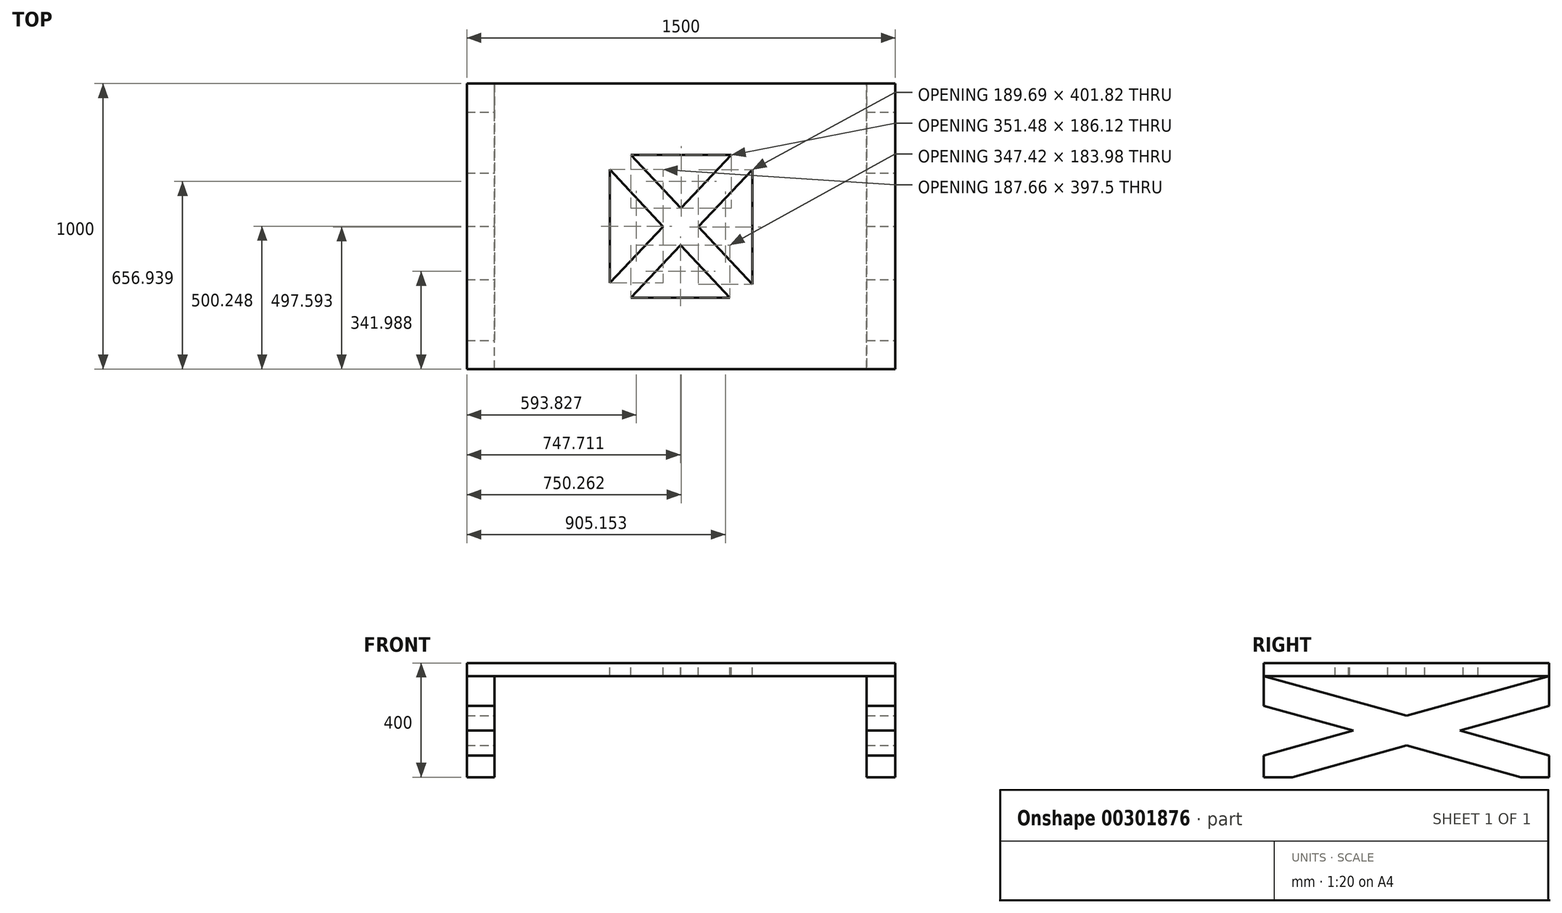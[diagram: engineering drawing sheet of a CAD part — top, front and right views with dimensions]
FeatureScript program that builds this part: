
annotation { "Feature Type Name" : "Feature", "Feature Type Description" : "" }
export const myFeature = defineFeature(function(context is Context, id is Id, definition is map)
    precondition{}
    {
        {
            var Q0;
            Q0=qCreatedBy(makeId("Front.planeOp"),FACE);
            var sketch = newSketch(context, id + "F0", { "sketchPlane" : qUnion([Q0])});
            skLineSegment(sketch, "E0.bottom", {"start": v(-768.36, 54.12) * mm, "end": v(731.64, 54.12) * mm});
            skLineSegment(sketch, "E0.top", {"start": v(-768.36, -345.88) * mm, "end": v(731.64, -345.88) * mm});
            skLineSegment(sketch, "E0.left", {"start": v(-768.36, 54.12) * mm, "end": v(-768.36, -345.88) * mm});
            skLineSegment(sketch, "E0.right", {"start": v(731.64, 54.12) * mm, "end": v(731.64, -345.88) * mm});
            skSolve(sketch);
        }
        {
            var Q0;
            Q0 = qSketchRegion(id + "F0", true);
            extrude(context, id + "F1", {"entities" : qUnion([Q0]), "depth" : 1000 * mm});
        }
        {
            var Q0;
            Q0=makeQuery(id+"F1.opExtrude","SWEPT_FACE",FACE,{"disambiguationData":[OSD([sQuery(id+"F0.wireOp",EDGE,"E0.right")])]});
            var sketch = newSketch(context, id + "F2", { "sketchPlane" : qUnion([Q0])});
            skLineSegment(sketch, "E1", {"start": v(-900, -345.88) * mm, "end": v(0, -95.88) * mm});
            skLineSegment(sketch, "E2", {"start": v(-1000, -269.87) * mm, "end": v(0, 7.9) * mm});
            skLineSegment(sketch, "E3", {"start": v(-100, -345.88) * mm, "end": v(-1000, -95.88) * mm});
            skLineSegment(sketch, "E4", {"start": v(0, -269.87) * mm, "end": v(-1000, 7.9) * mm});
            skLineSegment(sketch, "E5", {"start": v(-1000, 7.9) * mm, "end": v(0, 7.9) * mm});
            skSolve(sketch);
        }
        {
            var Q0;
            {var subQ0=sQuery(id+"F2.wireOp",EDGE,"E5");Q0=makeQuery(id+"F2.imprint","IMPRINT",FACE,{"disambiguationData":[TD([[makeQuery(id+"F2.imprint","IMPRINT",EDGE,{"derivedFrom":subQ0}),-1.0]])]});}
            var Q1;
            {var subQ0=sQuery(id+"F2.wireOp",EDGE,"E1");var subQ3=sQuery(id+"F2.wireOp",EDGE,"E3");var subQ4=makeQuery(id+"F2.imprint","INTERSECT",VERTEX,{"derivedFrom":[subQ0,subQ3]});Q1=makeQuery(id+"F2.imprint","IMPRINT",FACE,{"disambiguationData":[TD([[makeQuery(id+"F2.imprint","IMPRINT",EDGE,{"disambiguationData":[TD([[subQ4,1.0]])],"derivedFrom":subQ0}),-1.0]])]});}
            var Q2;
            {var subQ0=sQuery(id+"F2.wireOp",EDGE,"E1");var subQ1=makeQuery(id+"F1.opExtrude","CAP_EDGE",EDGE,{"disambiguationData":[OSD([sQuery(id+"F0.wireOp",EDGE,"E0.right")])],"isStart":true});var subQ2=makeQuery(id+"F2.imprint","INTERSECT",VERTEX,{"derivedFrom":[subQ1,subQ0]});Q2=makeQuery(id+"F2.imprint","IMPRINT",FACE,{"disambiguationData":[TD([[makeQuery(id+"F2.imprint","IMPRINT",EDGE,{"disambiguationData":[TD([[subQ2,1.0]])],"derivedFrom":subQ0}),-1.0]])]});}
            var Q3;
            {var subQ0=sQuery(id+"F2.wireOp",EDGE,"E2");var subQ1=makeQuery(id+"F1.opExtrude","CAP_EDGE",EDGE,{"disambiguationData":[OSD([sQuery(id+"F0.wireOp",EDGE,"E0.right")])],"isStart":false});var subQ2=makeQuery(id+"F2.imprint","INTERSECT",VERTEX,{"derivedFrom":[subQ1,subQ0]});Q3=makeQuery(id+"F2.imprint","IMPRINT",FACE,{"disambiguationData":[TD([[makeQuery(id+"F2.imprint","IMPRINT",EDGE,{"disambiguationData":[TD([[subQ2,-1.0]])],"derivedFrom":subQ0}),1.0]])]});}
            extrude(context, id + "F3", {"entities" : qUnion([Q0, Q1, Q2, Q3]), "operationType" : NewBodyOperationType.REMOVE, "endBound" : BoundingType.THROUGH_ALL, "oppositeDirection" : true, "depth" : 150 * mm});
        }
        {
            var Q0;
            Q0=makeQuery(id+"F1.opExtrude","CAP_FACE",FACE,{"disambiguationData":[OSD([sQuery(id+"F0.wireOp",EDGE,"E0.bottom"),sQuery(id+"F0.wireOp",EDGE,"E0.top"),sQuery(id+"F0.wireOp",EDGE,"E0.left"),sQuery(id+"F0.wireOp",EDGE,"E0.right")])],"isStart":false});
            var sketch = newSketch(context, id + "F4", { "sketchPlane" : qUnion([Q0])});
            skLineSegment(sketch, "E6", {"start": v(631.64, -345.88) * mm, "end": v(631.64, 8.12) * mm});
            skLineSegment(sketch, "E7", {"start": v(631.64, 8.12) * mm, "end": v(-668.36, 8.12) * mm});
            skLineSegment(sketch, "E8", {"start": v(-668.36, 8.12) * mm, "end": v(-668.36, -345.88) * mm});
            skSolve(sketch);
        }
        {
            var Q0;
            {var subQ0=sQuery(id+"F0.wireOp",EDGE,"E0.bottom");var subQ1=sQuery(id+"F0.wireOp",EDGE,"E0.right");var subQ2=sQuery(id+"F0.wireOp",EDGE,"E0.left");Q0=makeQuery(id+"F3.boolean.opBoolean","SPLIT",FACE,{"disambiguationData":[TD([makeQuery(id+"F1.opExtrude","SWEPT_FACE",FACE,{"disambiguationData":[OSD([subQ0])]})])],"derivedFrom":makeQuery(id+"F1.opExtrude","CAP_FACE",FACE,{"disambiguationData":[OSD([subQ0,sQuery(id+"F0.wireOp",EDGE,"E0.top"),subQ2,subQ1])],"isStart":true})});}
            var sketch = newSketch(context, id + "F5", { "sketchPlane" : qUnion([Q0])});
            skLineSegment(sketch, "E9.bottom", {"start": v(-631.78, 7.9) * mm, "end": v(672.17, 7.9) * mm});
            skLineSegment(sketch, "E9.top", {"start": v(-631.78, -349.34) * mm, "end": v(672.17, -349.34) * mm});
            skLineSegment(sketch, "E9.left", {"start": v(-631.78, 7.9) * mm, "end": v(-631.78, -349.34) * mm});
            skLineSegment(sketch, "E9.right", {"start": v(672.17, 7.9) * mm, "end": v(672.17, -349.34) * mm});
            skSolve(sketch);
        }
        {
            var Q0;
            Q0=makeQuery(id+"F5.imprint","IMPRINT",FACE,{"disambiguationData":[TD([[makeQuery(id+"F5.imprint","IMPRINT",EDGE,{"derivedFrom":sQuery(id+"F5.wireOp",EDGE,"E9.bottom")}),1.0]])]});
            extrude(context, id + "F6", {"entities" : qUnion([Q0]), "operationType" : NewBodyOperationType.REMOVE, "endBound" : BoundingType.THROUGH_ALL, "oppositeDirection" : true, "depth" : 25 * mm});
        }
        {
            var Q0;
            Q0=makeQuery(id+"F1.opExtrude","SWEPT_FACE",FACE,{"disambiguationData":[OSD([sQuery(id+"F0.wireOp",EDGE,"E0.bottom")])]});
            var sketch = newSketch(context, id + "F7", { "sketchPlane" : qUnion([Q0])});
            skLineSegment(sketch, "E10.bottom", {"start": v(231.64, -250) * mm, "end": v(-268.36, -250) * mm});
            skLineSegment(sketch, "E10.top", {"start": v(231.64, -750) * mm, "end": v(-268.36, -750) * mm});
            skLineSegment(sketch, "E10.left", {"start": v(231.64, -250) * mm, "end": v(231.64, -750) * mm});
            skLineSegment(sketch, "E10.right", {"start": v(-268.36, -250) * mm, "end": v(-268.36, -750) * mm});
            skLineSegment(sketch, "E11", {"start": v(231.64, -301.5) * mm, "end": v(-194.36, -750) * mm});
            skLineSegment(sketch, "E12", {"start": v(157.64, -250) * mm, "end": v(-268.36, -698.5) * mm});
            skLineSegment(sketch, "E13", {"start": v(-193.84, -250) * mm, "end": v(231.64, -703.32) * mm});
            skLineSegment(sketch, "E14", {"start": v(-268.36, -301) * mm, "end": v(153.06, -750) * mm});
            skSolve(sketch);
        }
        {
            var Q0;
            {var subQ0=sQuery(id+"F7.wireOp",EDGE,"E11");var subQ1=sQuery(id+"F7.wireOp",EDGE,"E10.left");var subQ2=makeQuery(id+"F7.imprint","INTERSECT",VERTEX,{"derivedFrom":[subQ1,subQ0]});Q0=makeQuery(id+"F7.imprint","IMPRINT",FACE,{"disambiguationData":[TD([[makeQuery(id+"F7.imprint","IMPRINT",EDGE,{"disambiguationData":[TD([[subQ2,-1.0]])],"derivedFrom":subQ1}),-1.0]])]});}
            var Q1;
            {var subQ0=sQuery(id+"F7.wireOp",EDGE,"E11");var subQ1=sQuery(id+"F7.wireOp",EDGE,"E10.top");var subQ2=makeQuery(id+"F7.imprint","INTERSECT",VERTEX,{"derivedFrom":[subQ1,subQ0]});Q1=makeQuery(id+"F7.imprint","IMPRINT",FACE,{"disambiguationData":[TD([[makeQuery(id+"F7.imprint","IMPRINT",EDGE,{"disambiguationData":[TD([[subQ2,1.0]])],"derivedFrom":subQ1}),-1.0]])]});}
            var Q2;
            {var subQ0=sQuery(id+"F7.wireOp",EDGE,"E12");var subQ1=sQuery(id+"F7.wireOp",EDGE,"E10.right");var subQ2=makeQuery(id+"F7.imprint","INTERSECT",VERTEX,{"derivedFrom":[subQ1,subQ0]});Q2=makeQuery(id+"F7.imprint","IMPRINT",FACE,{"disambiguationData":[TD([[makeQuery(id+"F7.imprint","IMPRINT",EDGE,{"disambiguationData":[TD([[subQ2,1.0]])],"derivedFrom":subQ1}),1.0]])]});}
            var Q3;
            {var subQ0=sQuery(id+"F7.wireOp",EDGE,"E12");var subQ1=sQuery(id+"F7.wireOp",EDGE,"E10.bottom");var subQ2=makeQuery(id+"F7.imprint","INTERSECT",VERTEX,{"derivedFrom":[subQ1,subQ0]});Q3=makeQuery(id+"F7.imprint","IMPRINT",FACE,{"disambiguationData":[TD([[makeQuery(id+"F7.imprint","IMPRINT",EDGE,{"disambiguationData":[TD([[subQ2,-1.0]])],"derivedFrom":subQ1}),1.0]])]});}
            extrude(context, id + "F8", {"entities" : qUnion([Q0, Q1, Q2, Q3]), "operationType" : NewBodyOperationType.REMOVE, "endBound" : BoundingType.THROUGH_ALL, "oppositeDirection" : true, "depth" : 25 * mm});
        }
    });
